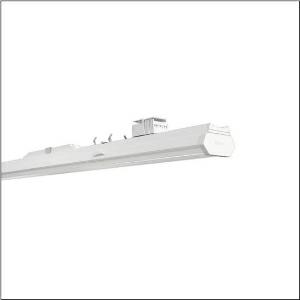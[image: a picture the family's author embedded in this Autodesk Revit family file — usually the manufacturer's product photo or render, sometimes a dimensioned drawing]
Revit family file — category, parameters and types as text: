
# Revit family: licross_r__11_protected_mo_51ts12vn475f_2d34
name_source: partatom
category: Lighting Fixtures
units: mm (PartAtom-declared; Revit-internal decimal feet)

## family parameters
Cut with Voids When Loaded = No
Host = Face
Light Source = No
Part Type = Normal
Room Calculation Point = No
Round Connector Dimension = Use Diameter
Shared = No

## types (1)
- --- (1 x LED, 7700 lm, 50.6 W, 4000K)
    Apparent Load = 51 VA
    CIE Flux Codes = 54 82 95 97 100
    Color Rendering = 80
    Color Temperature = 4000K
    Default Elevation = 1800 mm
    Description = Licross® 11 Protected MOluminaire insert, length: 1.500mm, width: 90mm, height: 101mm, LED rated luminous flux: 7.700lm, light colour: 840, control gear: DALI 2, CLO, control gear: ECG DALI, with plug, 5-pole, with phase selection, mains connection: 220..240V, AC, 50/60Hz, halogen-free wiring, primary optical cover: cover, of PMMA, light emission: direct with ceiling illumination distribution, protection rating (complete): IP50, insulation class (complete): insulation class I (protective earthing), certification: CE, ENEC, VDE, UKCA, protection symbol: D if used in an environment with non-conductive dust loads with corresponding accessories, permissible ambient temperature for indoor applications: -25..+35°C, corresponds to IFS (International Featured Standards) requirements for safety and quality in the food industry, reducing of maximum allowable ambient temperature of 5°C with ceiling mounting, packaging unit: 1 piece
    Height = 92 mm
    Lamp = 1 x LED
    Lamp Light Flux = 7700 lm
    Lamp Power = 50.6 W
    Lamp count = 1
    Length = 1500 mm
    Luminous efficacy = 152 lm/W
    Manufacturer = Siteco
    ModVariant = No
    Model = 51TS12VN475F
    Mounting Place = Ceiling
    Mounting Type = Pendant
    Number of Poles = 1
    OnlyDefault = Yes
    Power Factor = 1
    Product Name = Licross® 11 Protected MO
    Product group = luminaire insert
    ProductGroupID = 902
    Protection Class = Protection class I
    Protection Degree = IP 50
    RLX_Detail_Level = 1
    RlxData = <blob elided: 24049 chars, md5=4f2ac4d3>
    Socket = socket
    Standby Power = 0 W
    System Light Flux = 7700 lm
    System Power = 51 W
    Type Comments = factory setting: luminous flux: 100 % | dim-lin: 254 | 334 mA
    Type Image = l_1256145.jpg
    URL = http://relux.com
    VarID = @adj_129491
    Voltage = 0 V
    Weight = 0.00 kg
    Width = 88 mm

## geometry (parser evidence)
native form markers: Blend x4, Sweep x11
no freeform markers — native parametric forms only
